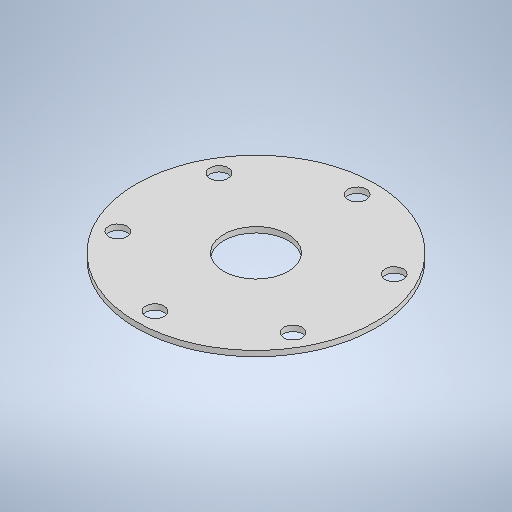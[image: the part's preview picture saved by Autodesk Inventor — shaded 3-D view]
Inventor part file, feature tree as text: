
AUTODESK INVENTOR PART (.ipt)
format: ipt  version: 2025 (Build 290162010, 162A)  size: 283,648 bytes
history: native  units: mm
features: sketch x3, other x3, sheet_metal_op x1, pattern_circular x1, extrude x1
ambient origin geometry x8: Origin, YZ Plane, XZ Plane, XY Plane, X Axis, Y Axis, Z Axis, Center Point
bodies: Solid1 (feature_tree)
feature tree (9):
  sheet_metal_op  "Face1"
  pattern_circular  "Circular Pattern1"  Count=13  [1 undecoded]
  extrude  "Extrusion1"  Depth=10.0mm
  sketch  "Sketch1"  dims[d1=3.0mm d2=10.0mm]
  other  "Plate1"
  sketch  "Sketch2"  dims[d3=55.0mm]
  sketch  "Sketch3"  dims[d4=3.0mm d5=0.0mm d6=60.0mm d7=360.0deg d9=35.0mm d10=0.0mm d11=0.0mm]
  other  "Cut1"
  other  "Definition1"
note: 1 required parameter value undecoded (feature->parameter linkage not recoverable at this tier; creation-order binding heuristic only, values carry confidence <= 0.55)
